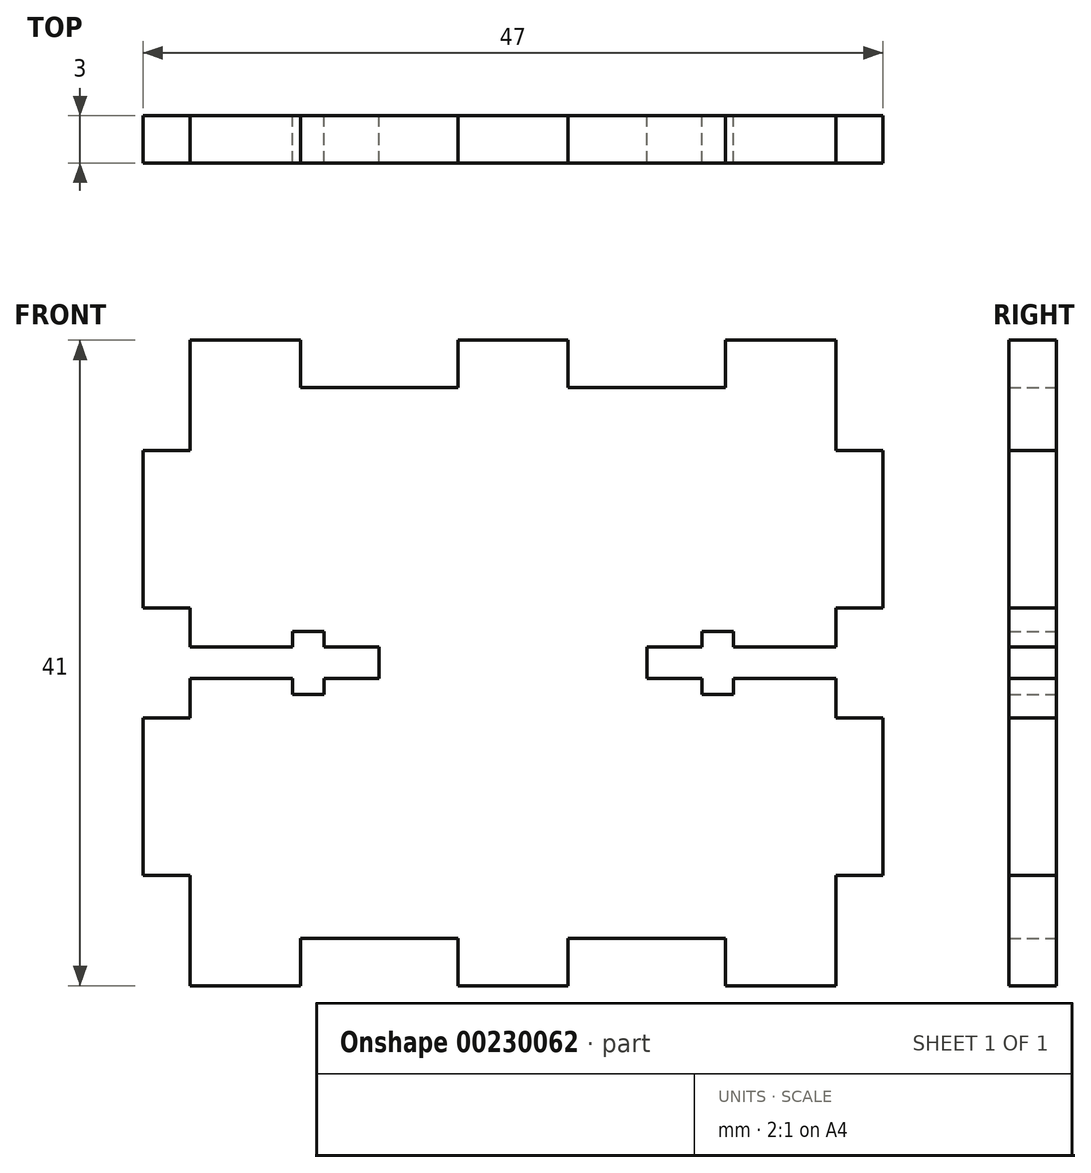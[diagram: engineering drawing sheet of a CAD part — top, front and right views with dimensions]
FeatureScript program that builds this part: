
annotation { "Feature Type Name" : "Feature", "Feature Type Description" : "" }
export const myFeature = defineFeature(function(context is Context, id is Id, definition is map)
    precondition{}
    {
        {
            var Q0;
            Q0=qCreatedBy(makeId("Front.planeOp"),FACE);
            var sketch = newSketch(context, id + "F0", { "sketchPlane" : qUnion([Q0])});
            skLineSegment(sketch, "E0", {"start": v(3, 0) * mm, "end": v(3, 7) * mm});
            skLineSegment(sketch, "E1", {"start": v(3, 7) * mm, "end": v(0, 7) * mm});
            skLineSegment(sketch, "E2", {"start": v(0, 7) * mm, "end": v(0, 17) * mm});
            skLineSegment(sketch, "E3", {"start": v(0, 17) * mm, "end": v(3, 17) * mm});
            skLineSegment(sketch, "E4", {"start": v(3, 24) * mm, "end": v(0, 24) * mm});
            skLineSegment(sketch, "E5", {"start": v(0, 24) * mm, "end": v(0, 34) * mm});
            skLineSegment(sketch, "E6", {"start": v(0, 34) * mm, "end": v(3, 34) * mm});
            skLineSegment(sketch, "E7", {"start": v(3, 34) * mm, "end": v(3, 41) * mm});
            skLineSegment(sketch, "E8", {"start": v(3, 41) * mm, "end": v(10, 41) * mm});
            skLineSegment(sketch, "E9", {"start": v(10, 41) * mm, "end": v(10, 38) * mm});
            skLineSegment(sketch, "E10", {"start": v(10, 38) * mm, "end": v(20, 38) * mm});
            skLineSegment(sketch, "E11", {"start": v(20, 38) * mm, "end": v(20, 41) * mm});
            skLineSegment(sketch, "E12", {"start": v(20, 41) * mm, "end": v(23.5, 41) * mm});
            skLineSegment(sketch, "E13", {"start": v(3, 17) * mm, "end": v(3, 19.5) * mm});
            skLineSegment(sketch, "E14.MirrorCS", {"start": v(27, 41) * mm, "end": v(23.5, 41) * mm});
            skLineSegment(sketch, "E15.MirrorCS", {"start": v(44, 0) * mm, "end": v(44, 7) * mm});
            skLineSegment(sketch, "E16.MirrorCS", {"start": v(44, 41) * mm, "end": v(37, 41) * mm});
            skLineSegment(sketch, "E17.MirrorCS", {"start": v(47, 17) * mm, "end": v(44, 17) * mm});
            skLineSegment(sketch, "E18.MirrorCS", {"start": v(44, 24) * mm, "end": v(47, 24) * mm});
            skLineSegment(sketch, "E19.MirrorCS", {"start": v(47, 7) * mm, "end": v(47, 17) * mm});
            skLineSegment(sketch, "E20.MirrorCS", {"start": v(37, 41) * mm, "end": v(37, 38) * mm});
            skLineSegment(sketch, "E21.MirrorCS", {"start": v(44, 17) * mm, "end": v(44, 19.5) * mm});
            skLineSegment(sketch, "E22.MirrorCS", {"start": v(47, 24) * mm, "end": v(47, 34) * mm});
            skLineSegment(sketch, "E23.MirrorCS", {"start": v(37, 38) * mm, "end": v(27, 38) * mm});
            skLineSegment(sketch, "E24.MirrorCS", {"start": v(47, 34) * mm, "end": v(44, 34) * mm});
            skLineSegment(sketch, "E25.MirrorCS", {"start": v(27, 38) * mm, "end": v(27, 41) * mm});
            skLineSegment(sketch, "E26.MirrorCS", {"start": v(44, 7) * mm, "end": v(47, 7) * mm});
            skLineSegment(sketch, "E27.MirrorCS", {"start": v(44, 34) * mm, "end": v(44, 41) * mm});
            skLineSegment(sketch, "E28", {"start": v(3, 20.5) * mm, "end": v(44, 20.5) * mm, "construction": true});
            skLineSegment(sketch, "E29.bottom", {"start": v(3, 21.5) * mm, "end": v(9.5, 21.5) * mm});
            skLineSegment(sketch, "E29.top", {"start": v(3, 19.5) * mm, "end": v(9.5, 19.5) * mm});
            skLineSegment(sketch, "E29.right", {"start": v(15, 21.5) * mm, "end": v(15, 19.5) * mm});
            skLineSegment(sketch, "E30.bottom", {"start": v(9.5, 22.5) * mm, "end": v(11.5, 22.5) * mm});
            skLineSegment(sketch, "E30.top", {"start": v(9.5, 18.5) * mm, "end": v(11.5, 18.5) * mm});
            skLineSegment(sketch, "E30.left", {"start": v(9.5, 22.5) * mm, "end": v(9.5, 21.5) * mm});
            skLineSegment(sketch, "E30.right", {"start": v(11.5, 22.5) * mm, "end": v(11.5, 21.5) * mm});
            skPoint(sketch, "E31.orphan", {"position": v(0, 21.5) * mm});
            skLineSegment(sketch, "E32.trimOffspring", {"start": v(3, 21.5) * mm, "end": v(3, 24) * mm});
            skLineSegment(sketch, "E33.trimOffspring", {"start": v(9.5, 19.5) * mm, "end": v(9.5, 18.5) * mm});
            skLineSegment(sketch, "E34.trimOffspring", {"start": v(11.5, 19.5) * mm, "end": v(15, 19.5) * mm});
            skLineSegment(sketch, "E35.trimOffspring", {"start": v(11.5, 19.5) * mm, "end": v(11.5, 18.5) * mm});
            skLineSegment(sketch, "E36.trimOffspring", {"start": v(11.5, 21.5) * mm, "end": v(15, 21.5) * mm});
            skLineSegment(sketch, "E37.bottom", {"start": v(32, 21.5) * mm, "end": v(35.5, 21.5) * mm});
            skLineSegment(sketch, "E37.top", {"start": v(32, 19.5) * mm, "end": v(35.5, 19.5) * mm});
            skLineSegment(sketch, "E37.left", {"start": v(32, 21.5) * mm, "end": v(32, 19.5) * mm});
            skLineSegment(sketch, "E38.bottom", {"start": v(35.5, 22.5) * mm, "end": v(37.5, 22.5) * mm});
            skLineSegment(sketch, "E38.top", {"start": v(35.5, 18.5) * mm, "end": v(37.5, 18.5) * mm});
            skLineSegment(sketch, "E38.left", {"start": v(35.5, 22.5) * mm, "end": v(35.5, 21.5) * mm});
            skLineSegment(sketch, "E38.right", {"start": v(37.5, 22.5) * mm, "end": v(37.5, 21.5) * mm});
            skLineSegment(sketch, "E39.trimOffspring", {"start": v(44, 21.5) * mm, "end": v(44, 24) * mm});
            skLineSegment(sketch, "E40.trimOffspring", {"start": v(37.5, 19.5) * mm, "end": v(37.5, 18.5) * mm});
            skLineSegment(sketch, "E41.trimOffspring", {"start": v(35.5, 19.5) * mm, "end": v(35.5, 18.5) * mm});
            skLineSegment(sketch, "E42.trimOffspring", {"start": v(37.5, 21.5) * mm, "end": v(44, 21.5) * mm});
            skLineSegment(sketch, "E43.trimOffspring", {"start": v(37.5, 19.5) * mm, "end": v(44, 19.5) * mm});
            skLineSegment(sketch, "E44", {"start": v(3, 0) * mm, "end": v(10, 0) * mm});
            skLineSegment(sketch, "E45", {"start": v(10, 0) * mm, "end": v(10, 3) * mm});
            skLineSegment(sketch, "E46", {"start": v(10, 3) * mm, "end": v(20, 3) * mm});
            skLineSegment(sketch, "E47", {"start": v(20, 3) * mm, "end": v(20, 0) * mm});
            skLineSegment(sketch, "E48", {"start": v(20, 0) * mm, "end": v(27, 0) * mm});
            skLineSegment(sketch, "E49", {"start": v(27, 0) * mm, "end": v(27, 3) * mm});
            skLineSegment(sketch, "E50", {"start": v(27, 3) * mm, "end": v(37, 3) * mm});
            skLineSegment(sketch, "E51", {"start": v(37, 3) * mm, "end": v(37, 0) * mm});
            skLineSegment(sketch, "E52", {"start": v(37, 0) * mm, "end": v(44, 0) * mm});
            skLineSegment(sketch, "E53", {"start": v(44, 24) * mm, "end": v(44, 21.5) * mm});
            skLineSegment(sketch, "E54.trimOffspring", {"start": v(3, 19.5) * mm, "end": v(3, 17) * mm});
            skLineSegment(sketch, "E55.trimOffspring", {"start": v(44, 20.5) * mm, "end": v(44, 17) * mm});
            skSolve(sketch);
        }
        {
            var Q0;
            Q0 = qSketchRegion(id + "F0", true);
            extrude(context, id + "F1", {"entities" : qUnion([Q0]), "depth" : 3 * mm});
        }
    });
